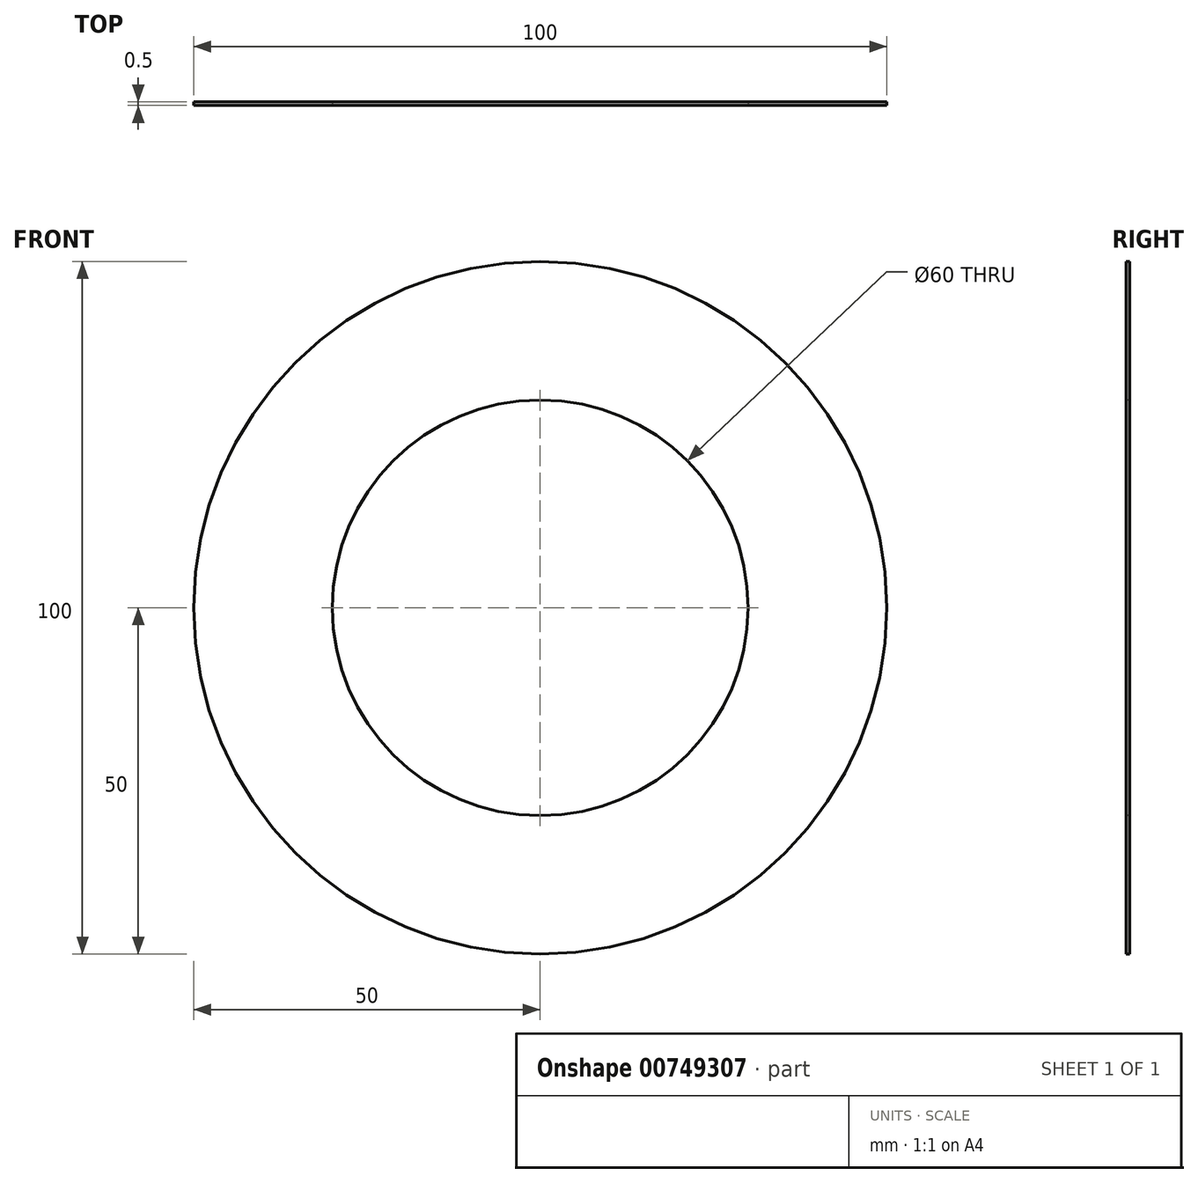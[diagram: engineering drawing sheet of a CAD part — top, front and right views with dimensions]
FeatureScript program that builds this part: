
annotation { "Feature Type Name" : "Feature", "Feature Type Description" : "" }
export const myFeature = defineFeature(function(context is Context, id is Id, definition is map)
    precondition{}
    {
        {
            var Q0;
            Q0=qCreatedBy(makeId("Front.planeOp"),FACE);
            var sketch = newSketch(context, id + "F0", { "sketchPlane" : qUnion([Q0])});
            skCircle(sketch, "E0", {"center": v(0, 0) * mm, "radius": 50 * mm});
            skSolve(sketch);
        }
        {
            var Q0;
            Q0=makeQuery(id+"F0.imprint","IMPRINT",FACE,{"disambiguationData":[TD([[makeQuery(id+"F0.imprint","IMPRINT",EDGE,{"derivedFrom":sQuery(id+"F0.wireOp",EDGE,"E0")}),1.0]])]});
            extrude(context, id + "F1", {"entities" : qUnion([Q0]), "oppositeDirection" : true, "depth" : 0.5 * mm, "offsetDistance" : 25 * mm});
        }
        {
            var Q0;
            Q0=makeQuery(id+"F1.opExtrude","CAP_FACE",FACE,{"disambiguationData":[OSD([sQuery(id+"F0.wireOp",EDGE,"E0")])],"isStart":true});
            var sketch = newSketch(context, id + "F2", { "sketchPlane" : qUnion([Q0])});
            skCircle(sketch, "E1", {"center": v(0, 0) * mm, "radius": 30 * mm});
            skSolve(sketch);
        }
        {
            var Q0;
            Q0=makeQuery(id+"F2.imprint","IMPRINT",FACE,{"disambiguationData":[TD([[makeQuery(id+"F2.imprint","IMPRINT",EDGE,{"derivedFrom":sQuery(id+"F2.wireOp",EDGE,"E1")}),1.0]])]});
            extrude(context, id + "F3", {"entities" : qUnion([Q0]), "operationType" : NewBodyOperationType.REMOVE, "oppositeDirection" : true, "depth" : 0.5 * mm, "offsetDistance" : 25 * mm});
        }
    });
